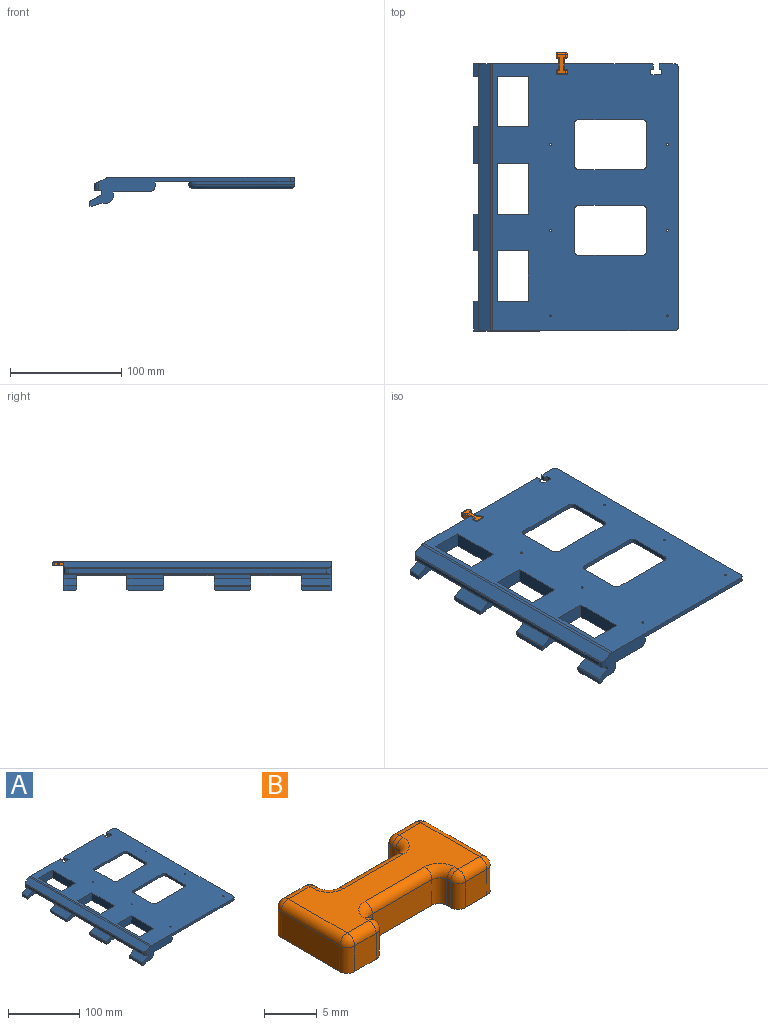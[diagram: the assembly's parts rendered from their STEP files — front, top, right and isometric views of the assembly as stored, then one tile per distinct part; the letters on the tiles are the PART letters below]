
ASSEMBLY  parts=2 mates=1
PART A: 152 faces, bbox 184.2x240x26.1 mm
  f0: plane 240x125mm, normal (0,0,-1), area 20631.7mm2, adj f1,f3,f4,f5,f6,f7,f8,f9
  f1: plane 180.14x26.08mm, normal (0,-1,0), area 1279.9mm2, adj f0,f35,f36,f45,f46,f47,f58,f59
  f2: plane 49.2x25.09mm, normal (0,-1,0), area 536.8mm2, adj f35,f37,f45,f48,f49,f56,f58,f65
  f3: plane 57x4mm, normal (0,-1,0), area 228mm2, adj f0,f35,f97,f100
  f4: plane 37x4mm, normal (-1,0,0), area 148mm2, adj f0,f35,f97,f98
  f5: plane 57x4mm, normal (0,1,0), area 228mm2, adj f0,f35,f98,f99
  f6: plane 57x4mm, normal (0,-1,0), area 228mm2, adj f0,f35,f93,f96
  f7: plane 37x4mm, normal (-1,0,0), area 148mm2, adj f0,f35,f93,f94
  f8: plane 57x4mm, normal (0,1,0), area 228mm2, adj f0,f35,f94,f95
  f9: plane 232x6mm, normal (1,0,0), area 1000mm2, adj f0,f35,f67,f68,f71,f72,f75,f76
  f10: plane 12.5x4mm, normal (0,1,0), area 50mm2, adj f0,f35,f102,f147
  f11: plane 4x3mm, normal (-1,0,0), area 12mm2, adj f0,f35,f147,f148
  f12: plane 4x0.5mm, normal (0,-1,0), area 2mm2, adj f0,f35,f148,f149
  f13: plane 4x3mm, normal (-1,0,0), area 12mm2, adj f0,f35,f149,f150
  f14: plane 8x4mm, normal (0,1,0), area 32mm2, adj f0,f35,f150,f151
  f15: plane 4x3mm, normal (1,0,0), area 12mm2, adj f0,f35,f136,f151
  f16: plane 4x0.5mm, normal (0,-1,0), area 2mm2, adj f0,f35,f136,f137
  f17: plane 4x3mm, normal (1,0,0), area 12mm2, adj f0,f35,f137,f138
  f18: plane 78x4mm, normal (0,1,0), area 312mm2, adj f0,f35,f138,f139
  f19: plane 4x3mm, normal (-1,0,0), area 12mm2, adj f0,f35,f139,f140
  f20: plane 4x0.5mm, normal (0,-1,0), area 2mm2, adj f0,f35,f140,f141
  f21: plane 4x3mm, normal (-1,0,0), area 12mm2, adj f0,f35,f141,f142
  f22: plane 8x4mm, normal (0,1,0), area 32mm2, adj f0,f35,f142,f143
  f23: plane 4x3mm, normal (1,0,0), area 12mm2, adj f0,f35,f143,f144
  f24: plane 4x0.5mm, normal (0,-1,0), area 2mm2, adj f0,f35,f144,f145
  f25: plane 4x3mm, normal (1,0,0), area 12mm2, adj f0,f35,f145,f146
  f26: plane 75.7x26.08mm, normal (0,1,0), area 861.9mm2, adj f0,f35,f36,f45,f48,f49,f58,f65
  f27: plane 37x4mm, normal (1,0,0), area 148mm2, adj f0,f35,f95,f96
  f28: cylinder r=0.9mm len=4mm, axis (0,0,1), area 22.6mm2, adj f0,f35
  f29: cylinder r=0.9mm len=4mm, axis (0,0,1), area 22.6mm2, adj f0,f35
  f30: cylinder r=0.9mm len=4mm, axis (0,0,1), area 22.6mm2, adj f0,f35
  f31: cylinder r=0.9mm len=4mm, axis (0,0,1), area 22.6mm2, adj f0,f35
  f32: cylinder r=0.9mm len=4mm, axis (0,0,1), area 22.6mm2, adj f0,f35
  f33: cylinder r=0.9mm len=4mm, axis (0,0,1), area 22.6mm2, adj f0,f35
  f34: plane 37x4mm, normal (1,0,0), area 148mm2, adj f0,f35,f99,f100
  f35: plane 240x166.82mm, normal (0,0,1), area 30245.3mm2, adj f1,f2,f3,f4,f5,f6,f7,f8
  f36: plane 240x3mm, normal (1,0,0), area 720mm2, adj f0,f1,f26,f116
  f37: plane 45.2x13mm, normal (-1,0,0), area 587.6mm2, adj f2,f35,f38,f45
  f38: plane 49.2x25.09mm, normal (0,1,0), area 536.8mm2, adj f35,f37,f45,f50,f51,f56,f58,f63
  f39: plane 49.2x25.09mm, normal (0,-1,0), area 536.8mm2, adj f35,f40,f45,f50,f51,f55,f58,f63
  f40: plane 45.2x13mm, normal (-1,0,0), area 587.6mm2, adj f35,f39,f41,f45
  f41: plane 49.14x25.09mm, normal (0,1,0), area 536.7mm2, adj f35,f40,f45,f52,f53,f55,f58,f61
  f42: plane 49.14x25.09mm, normal (0,-1,0), area 536.7mm2, adj f35,f43,f45,f52,f53,f54,f58,f61
  f43: plane 45.2x13mm, normal (-1,0,0), area 587.6mm2, adj f35,f42,f44,f45
  f44: plane 49.14x25.09mm, normal (0,1,0), area 536.7mm2, adj f35,f43,f45,f46,f47,f54,f58,f59
  f45: plane 240x32mm, normal (0,0,-1), area 3883.2mm2, adj f1,f2,f26,f37,f38,f39,f40,f41
  f46: plane 26.8x4mm, normal (1,0,0), area 107.2mm2, adj f1,f44,f45,f115
  f47: plane 26.8x4mm, normal (0,0,-1), area 107.2mm2, adj f1,f44,f115,f125
  f48: plane 11.4x4mm, normal (1,0,0), area 45.6mm2, adj f2,f26,f45,f114
  f49: plane 11.4x4mm, normal (0,0,-1), area 45.6mm2, adj f2,f26,f114,f122
  f50: plane 33.1x4mm, normal (1,0,0), area 132.4mm2, adj f38,f39,f45,f113
  f51: plane 33.1x4mm, normal (0,0,-1), area 132.4mm2, adj f38,f39,f113,f123
  f52: plane 33.1x4mm, normal (1,0,0), area 132.4mm2, adj f41,f42,f45,f112
  f53: plane 33.1x4mm, normal (0,0,-1), area 132.4mm2, adj f41,f42,f112,f124
  f54: plane 45.2x11.5mm, normal (1,0,0), area 519.8mm2, adj f35,f42,f44,f58
  f55: plane 45.2x11.5mm, normal (1,0,0), area 519.8mm2, adj f35,f39,f41,f58
  f56: plane 45.2x11.5mm, normal (1,0,0), area 519.8mm2, adj f2,f35,f38,f58
  f57: plane 232x3.88mm, normal (-1,0,0), area 900.6mm2, adj f91,f92,f128,f129
  f58: plane 240x16mm, normal (0,0,-1), area 2793.5mm2, adj f1,f2,f26,f38,f39,f41,f42,f44
  f59: plane 26.8x4mm, normal (-1,0,0), area 107.2mm2, adj f1,f44,f58,f60
  f60: plane 26.8x0.34mm, normal (0,0,1), area 9.2mm2, adj f1,f44,f59,f108
  f61: plane 33.1x4mm, normal (-1,0,0), area 132.4mm2, adj f41,f42,f58,f62
  f62: plane 33.1x0.34mm, normal (0,0,1), area 11.3mm2, adj f41,f42,f61,f109
  f63: plane 33.1x4mm, normal (-1,0,0), area 132.4mm2, adj f38,f39,f58,f64
  f64: plane 33.1x0.34mm, normal (0,0,1), area 11.3mm2, adj f38,f39,f63,f110
  f65: plane 11.4x0.34mm, normal (0,0,1), area 3.9mm2, adj f2,f26,f66,f111
  f66: plane 11.4x4mm, normal (-1,0,0), area 45.6mm2, adj f2,f26,f58,f65
  f67: plane 89x2mm, normal (0,1,0), area 178mm2, adj f0,f9,f69,f90
  f68: plane 89x2mm, normal (0,-1,0), area 178mm2, adj f0,f9,f69,f87
  f69: cylinder r=6mm len=12mm, axis (0,0,1), area 37.7mm2, adj f0,f67,f68,f89
  f70: plane 87x4mm, normal (0,0,-1), area 346.3mm2, adj f87,f88,f89,f90
  f71: plane 89x2mm, normal (0,-1,0), area 178mm2, adj f0,f9,f73,f83
  f72: plane 89x2mm, normal (0,1,0), area 178mm2, adj f0,f9,f73,f86
  f73: cylinder r=6mm len=12mm, axis (0,0,1), area 37.7mm2, adj f0,f71,f72,f85
  f74: plane 87x4mm, normal (0,0,-1), area 346.3mm2, adj f83,f84,f85,f86
  f75: plane 89x2mm, normal (0,-1,0), area 178mm2, adj f0,f9,f77,f80
  f76: plane 89x2mm, normal (0,1,0), area 178mm2, adj f0,f9,f77,f81
  f77: cylinder r=6mm len=12mm, axis (0,0,1), area 37.7mm2, adj f0,f75,f76,f79
  f78: plane 87x4mm, normal (0,0,-1), area 346.3mm2, adj f79,f80,f81,f82
  f79: torus R=2mm, axis (0,0,1), area 89.7mm2, adj f77,f78,f80,f81
  f80: cylinder r=4mm len=89mm, axis (-1,0,0), area 550.1mm2, adj f75,f78,f79,f82
  f81: cylinder r=4mm len=89mm, axis (1,0,0), area 550.1mm2, adj f76,f78,f79,f82
  f82: cylinder r=4mm len=12mm, axis (0,-1,0), area 57.1mm2, adj f9,f78,f80,f81
  f83: cylinder r=4mm len=89mm, axis (-1,0,0), area 550.1mm2, adj f71,f74,f84,f85
  f84: cylinder r=4mm len=12mm, axis (0,-1,0), area 57.1mm2, adj f9,f74,f83,f86
  f85: torus R=2mm, axis (0,0,1), area 89.7mm2, adj f73,f74,f83,f86
  f86: cylinder r=4mm len=89mm, axis (1,0,0), area 550.1mm2, adj f72,f74,f84,f85
  f87: cylinder r=4mm len=89mm, axis (-1,0,0), area 550.1mm2, adj f68,f70,f88,f89
  f88: cylinder r=4mm len=12mm, axis (0,-1,0), area 57.1mm2, adj f9,f70,f87,f90
  f89: torus R=2mm, axis (0,0,1), area 89.7mm2, adj f69,f70,f87,f90
  f90: cylinder r=4mm len=89mm, axis (1,0,0), area 550.1mm2, adj f67,f70,f88,f89
  f91: cylinder r=4mm len=7.5mm, axis (0,0,1), area 37.4mm2, adj f1,f57,f58,f103,f128,f129
  f92: cylinder r=4mm len=7.5mm, axis (0,0,-1), area 37.4mm2, adj f26,f57,f58,f103,f128,f129
  f93: cylinder r=4mm len=4mm, axis (0,0,-1), area 25.1mm2, adj f0,f6,f7,f35
  f94: cylinder r=4mm len=4mm, axis (0,0,1), area 25.1mm2, adj f0,f7,f8,f35
  f95: cylinder r=4mm len=4mm, axis (0,0,-1), area 25.1mm2, adj f0,f8,f27,f35
  f96: cylinder r=4mm len=4mm, axis (0,0,1), area 25.1mm2, adj f0,f6,f27,f35
  f97: cylinder r=4mm len=4mm, axis (0,0,-1), area 25.1mm2, adj f0,f3,f4,f35
  f98: cylinder r=4mm len=4mm, axis (0,0,1), area 25.1mm2, adj f0,f4,f5,f35
  f99: cylinder r=4mm len=4mm, axis (0,0,-1), area 25.1mm2, adj f0,f5,f34,f35
  f100: cylinder r=4mm len=4mm, axis (0,0,1), area 25.1mm2, adj f0,f3,f34,f35
  f101: cylinder r=4mm len=4mm, axis (0,0,-1), area 25.1mm2, adj f0,f1,f9,f35
  f102: cylinder r=4mm len=4mm, axis (0,0,1), area 25.1mm2, adj f0,f9,f10,f35
  f103: plane 240x10.39mm, normal (-0.45,0,0.89), area 2783.9mm2, adj f1,f26,f91,f92,f121,f128
  f104: plane 11.4x4.52mm, normal (-1,0,-0.1), area 51.2mm2, adj f2,f26,f111,f117,f130
  f105: plane 33.1x4.52mm, normal (-1,0,-0.1), area 149.2mm2, adj f38,f39,f110,f118,f131,f132
  f106: plane 33.1x3.86mm, normal (-1,0,-0.1), area 127.5mm2, adj f41,f42,f119,f126,f133,f134
  f107: plane 26.8x3.86mm, normal (-1,0,-0.1), area 103.5mm2, adj f1,f44,f120,f127,f135
  f108: plane 26.8x10.28mm, normal (-0.49,0,0.87), area 315.8mm2, adj f1,f44,f60,f127
  f109: plane 33.1x10.28mm, normal (-0.49,0,0.87), area 390mm2, adj f41,f42,f62,f126
  f110: plane 33.1x10.86mm, normal (-0.49,0,0.87), area 411.7mm2, adj f38,f39,f64,f105
  f111: plane 11.4x10.86mm, normal (-0.49,0,0.87), area 141.8mm2, adj f2,f26,f65,f104
  f112: cylinder r=6mm len=33.1mm, axis (0,-1,0), area 312mm2, adj f41,f42,f52,f53
  f113: cylinder r=6mm len=33.1mm, axis (0,-1,0), area 312mm2, adj f38,f39,f50,f51
  f114: cylinder r=6mm len=11.4mm, axis (0,-1,0), area 107.4mm2, adj f2,f26,f48,f49
  f115: cylinder r=6mm len=26.8mm, axis (0,-1,0), area 252.6mm2, adj f1,f44,f46,f47
  f116: cylinder r=6mm len=240mm, axis (0,-1,0), area 2261.9mm2, adj f1,f26,f36,f45
  f117: plane 10.4x1mm, normal (0.1,0,-1), area 10.4mm2, adj f26,f104,f122,f130
  f118: plane 31.1x1mm, normal (0.1,0,-1), area 31.1mm2, adj f105,f123,f131,f132
  f119: plane 31.1x1mm, normal (0.1,0,-1), area 31.1mm2, adj f106,f124,f133,f134
  f120: plane 25.8x1mm, normal (0.1,0,-1), area 25.8mm2, adj f1,f107,f125,f135
  f121: cylinder r=5mm len=240mm, axis (0,-1,0), area 556.4mm2, adj f1,f26,f35,f103
  f122: plane 11.4x9.75mm, normal (0.29,0,-0.96), area 113.7mm2, adj f2,f26,f49,f117,f130
  f123: plane 33.1x9.75mm, normal (0.29,0,-0.96), area 332.5mm2, adj f38,f39,f51,f118,f131,f132
  f124: plane 33.1x9.75mm, normal (0.29,0,-0.96), area 332.5mm2, adj f41,f42,f53,f119,f133,f134
  f125: plane 26.8x9.75mm, normal (0.29,0,-0.96), area 270.8mm2, adj f1,f44,f47,f120,f135
  f126: cylinder r=1mm len=33.1mm, axis (0,-1,0), area 38.4mm2, adj f41,f42,f106,f109
  f127: cylinder r=1mm len=26.8mm, axis (0,-1,0), area 31.1mm2, adj f1,f44,f107,f108
  f128: cylinder r=1mm len=236.06mm, axis (0,-1,0), area 259.1mm2, adj f57,f91,f92,f103
  f129: cylinder r=1mm len=237.29mm, axis (0,1,0), area 368.6mm2, adj f57,f58,f91,f92
  f130: plane 5.97x1.59mm, normal (0.07,-0.71,-0.7), area 4.9mm2, adj f2,f104,f117,f122
  f131: plane 5.97x1.59mm, normal (0.07,0.71,-0.7), area 4.9mm2, adj f38,f105,f118,f123
  f132: plane 5.97x1.59mm, normal (0.07,-0.71,-0.7), area 4.9mm2, adj f39,f105,f118,f123
  f133: plane 5.97x1.59mm, normal (0.07,0.71,-0.7), area 4.9mm2, adj f41,f106,f119,f124
  f134: plane 5.97x1.59mm, normal (0.07,-0.71,-0.7), area 4.9mm2, adj f42,f106,f119,f124
  f135: plane 5.97x1.59mm, normal (0.07,0.71,-0.7), area 4.9mm2, adj f44,f107,f120,f125
  f136: cylinder r=1mm len=4mm, axis (0,0,1), area 6.3mm2, adj f0,f15,f16,f35
  f137: cylinder r=1mm len=4mm, axis (0,0,-1), area 6.3mm2, adj f0,f16,f17,f35
  f138: cylinder r=1mm len=4mm, axis (0,0,-1), area 6.3mm2, adj f0,f17,f18,f35
  f139: cylinder r=1mm len=4mm, axis (0,0,1), area 6.3mm2, adj f0,f18,f19,f35
  f140: cylinder r=1mm len=4mm, axis (0,0,1), area 6.3mm2, adj f0,f19,f20,f35
  f141: cylinder r=1mm len=4mm, axis (0,0,-1), area 6.3mm2, adj f0,f20,f21,f35
  f142: cylinder r=1mm len=4mm, axis (0,0,1), area 6.3mm2, adj f0,f21,f22,f35
  f143: cylinder r=1mm len=4mm, axis (0,0,-1), area 6.3mm2, adj f0,f22,f23,f35
  f144: cylinder r=1mm len=4mm, axis (0,0,1), area 6.3mm2, adj f0,f23,f24,f35
  f145: cylinder r=1mm len=4mm, axis (0,0,-1), area 6.3mm2, adj f0,f24,f25,f35
  f146: cylinder r=1mm len=4mm, axis (0,0,-1), area 6.3mm2, adj f0,f25,f26,f35
  f147: cylinder r=1mm len=4mm, axis (0,0,1), area 6.3mm2, adj f0,f10,f11,f35
  f148: cylinder r=1mm len=4mm, axis (0,0,1), area 6.3mm2, adj f0,f11,f12,f35
  f149: cylinder r=1mm len=4mm, axis (0,0,-1), area 6.3mm2, adj f0,f12,f13,f35
  f150: cylinder r=1mm len=4mm, axis (0,0,1), area 6.3mm2, adj f0,f13,f14,f35
  f151: cylinder r=1mm len=4mm, axis (0,0,-1), area 6.3mm2, adj f0,f14,f15,f35
PART B: 50 faces, bbox 19.8x9.9x4 mm
  f0: plane 3x2.9mm, normal (0,-1,0), area 8.7mm2, adj f12,f40,f46,f49
  f1: plane 3x0.5mm, normal (1,0,0), area 1.5mm2, adj f12,f43,f47,f49
  f2: plane 8x3mm, normal (0,-1,0), area 24mm2, adj f12,f37,f42,f43
  f3: plane 3x0.5mm, normal (-1,0,0), area 1.5mm2, adj f12,f31,f36,f37
  f4: plane 3x2.9mm, normal (0,-1,0), area 8.7mm2, adj f12,f25,f30,f31
  f5: plane 7.9x3mm, normal (1,0,0), area 23.7mm2, adj f12,f19,f24,f25
  f6: plane 3x2.9mm, normal (0,1,0), area 8.7mm2, adj f12,f14,f18,f19
  f7: plane 3x0.5mm, normal (-1,0,0), area 1.5mm2, adj f12,f14,f16,f17
  f8: plane 8x3mm, normal (0,1,0), area 24mm2, adj f12,f16,f22,f23
  f9: plane 3x0.5mm, normal (1,0,0), area 1.5mm2, adj f12,f22,f28,f29
  f10: plane 3x2.9mm, normal (0,1,0), area 8.7mm2, adj f12,f28,f34,f35
  f11: plane 7.9x3mm, normal (-1,0,0), area 23.7mm2, adj f12,f34,f40,f41
  f12: plane 19.8x9.9mm, normal (0,0,-1), area 145.2mm2, adj f0,f1,f2,f3,f4,f5,f6,f7
  f13: plane 17.8x7.9mm, normal (0,0,1), area 84.1mm2, adj f17,f18,f20,f23,f24,f26,f29,f30
  f14: cylinder r=1mm len=3mm, axis (0,0,1), area 4.7mm2, adj f6,f7,f12,f15
  f15: sphere r=1mm, area 1.6mm2, adj f14,f17,f18
  f16: cylinder r=1mm len=3mm, axis (0,0,1), area 4.7mm2, adj f7,f8,f12,f20
  f17: cylinder r=1mm len=1mm, axis (0,-1,0), area 0.8mm2, adj f7,f13,f15,f20
  f18: cylinder r=1mm len=2.9mm, axis (-1,0,0), area 4.6mm2, adj f6,f13,f15,f21
  f19: cylinder r=1mm len=3mm, axis (0,0,1), area 4.7mm2, adj f5,f6,f12,f21
  f20: torus R=2mm, axis (0,0,1), area 3.4mm2, adj f13,f16,f17,f23
  f21: sphere r=1mm, area 1.6mm2, adj f18,f19,f24
  f22: cylinder r=1mm len=3mm, axis (0,0,-1), area 4.7mm2, adj f8,f9,f12,f26
  f23: cylinder r=1mm len=8mm, axis (-1,0,0), area 12.6mm2, adj f8,f13,f20,f26
  f24: cylinder r=1mm len=7.9mm, axis (0,1,0), area 12.4mm2, adj f5,f13,f21,f27
  f25: cylinder r=1mm len=3mm, axis (0,0,1), area 4.7mm2, adj f4,f5,f12,f27
  f26: torus R=2mm, axis (0,0,1), area 3.4mm2, adj f13,f22,f23,f29
  f27: sphere r=1mm, area 1.6mm2, adj f24,f25,f30
  f28: cylinder r=1mm len=3mm, axis (0,0,1), area 4.7mm2, adj f9,f10,f12,f32
  f29: cylinder r=1mm len=1mm, axis (0,1,0), area 0.8mm2, adj f9,f13,f26,f32
  f30: cylinder r=1mm len=2.9mm, axis (1,0,0), area 4.6mm2, adj f4,f13,f27,f33
  f31: cylinder r=1mm len=3mm, axis (0,0,1), area 4.7mm2, adj f3,f4,f12,f33
  f32: sphere r=1mm, area 1.6mm2, adj f28,f29,f35
  f33: sphere r=1mm, area 1.6mm2, adj f30,f31,f36
  f34: cylinder r=1mm len=3mm, axis (0,0,1), area 4.7mm2, adj f10,f11,f12,f38
  f35: cylinder r=1mm len=2.9mm, axis (-1,0,0), area 4.6mm2, adj f10,f13,f32,f38
  f36: cylinder r=1mm len=1mm, axis (0,-1,0), area 0.8mm2, adj f3,f13,f33,f39
  f37: cylinder r=1mm len=3mm, axis (0,0,-1), area 4.7mm2, adj f2,f3,f12,f39
  f38: sphere r=1mm, area 1.6mm2, adj f34,f35,f41
  f39: torus R=2mm, axis (0,0,1), area 3.4mm2, adj f13,f36,f37,f42
  f40: cylinder r=1mm len=3mm, axis (0,0,1), area 4.7mm2, adj f0,f11,f12,f44
  f41: cylinder r=1mm len=7.9mm, axis (0,-1,0), area 12.4mm2, adj f11,f13,f38,f44
  f42: cylinder r=1mm len=8mm, axis (1,0,0), area 12.6mm2, adj f2,f13,f39,f45
  f43: cylinder r=1mm len=3mm, axis (0,0,1), area 4.7mm2, adj f1,f2,f12,f45
  f44: sphere r=1mm, area 1.6mm2, adj f40,f41,f46
  f45: torus R=2mm, axis (0,0,1), area 3.4mm2, adj f13,f42,f43,f47
  f46: cylinder r=1mm len=2.9mm, axis (1,0,0), area 4.6mm2, adj f0,f13,f44,f48
  f47: cylinder r=1mm len=1mm, axis (0,1,0), area 0.8mm2, adj f1,f13,f45,f48
  f48: sphere r=1mm, area 1.6mm2, adj f46,f47,f49
  f49: cylinder r=1mm len=3mm, axis (0,0,1), area 4.7mm2, adj f0,f1,f12,f48
PLACE A t=(-94.09,68.05,-59.53)mm fixed
PLACE B rot(axis=(0,0,-1),90deg) t=(-19.14,67.95,-59.52)mm
MATE slider B.f25 <-> A.f143  axis (0,0,1) through (-23.09,59.05,-62.02)mm
